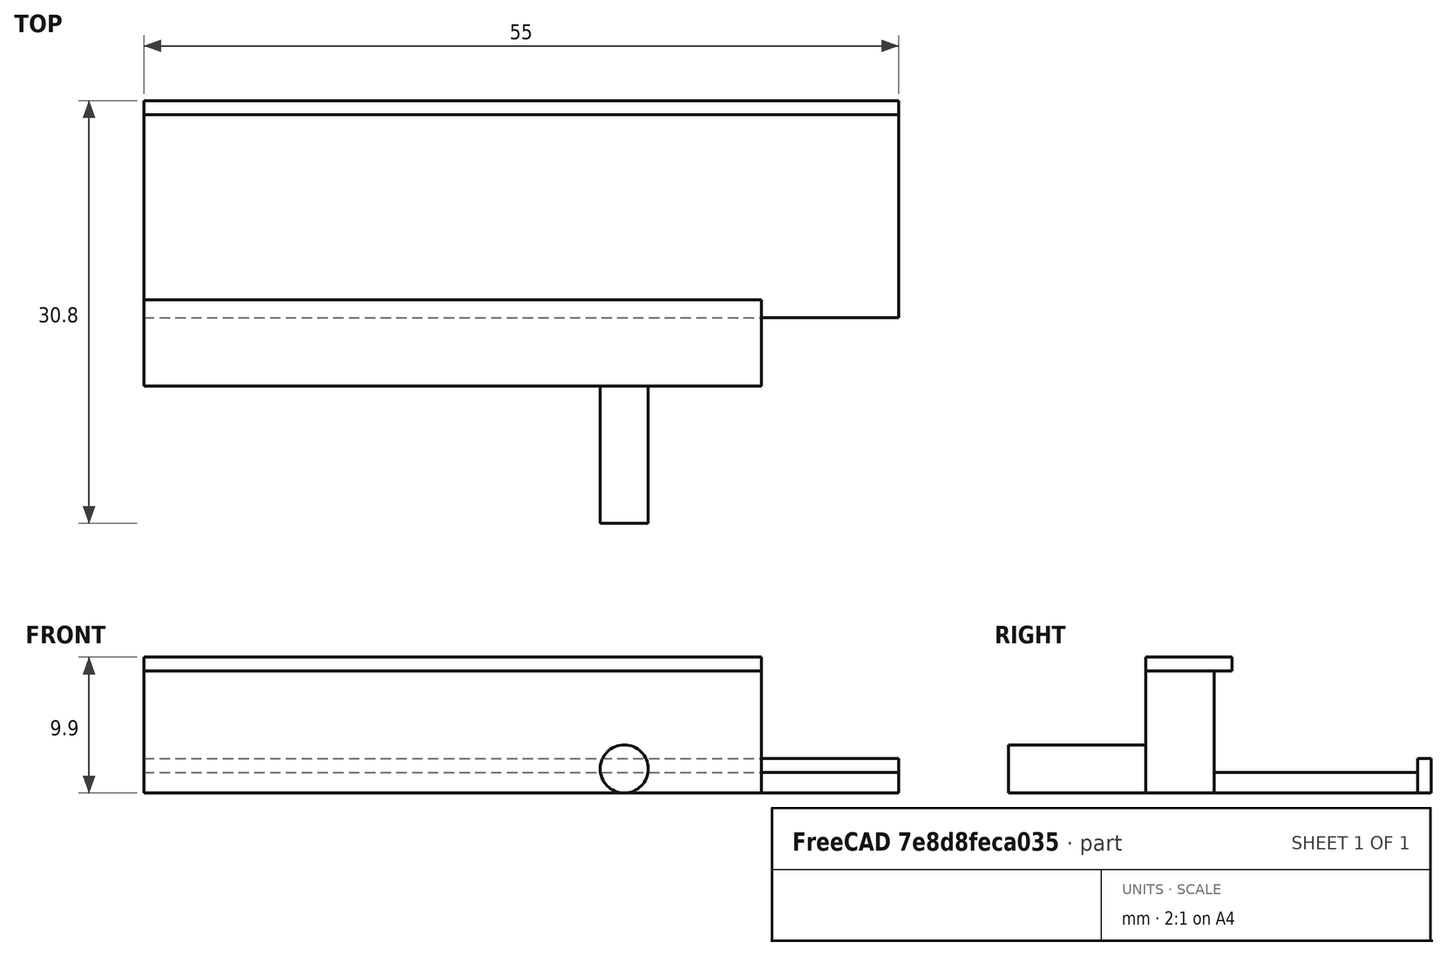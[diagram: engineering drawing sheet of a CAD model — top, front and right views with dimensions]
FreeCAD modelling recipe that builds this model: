
FCSTD DOCUMENT  (FreeCAD 0.21R33771 (Git))
Label: usb-support-1
License: All rights reserved
LicenseURL: http://en.wikipedia.org/wiki/All_rights_reserved
objects: Part::Box×4, Part::Cylinder×1
note: 5 computed .brp shape members not serialized (recipe doc carries the construction recipe); baked Part::Feature solids carry a one-line shape summary decoded from their .brp

FEATURE [Part::Box] Box  label="Cube"
  AttacherType = Attacher::AttachEngine3D
  Height = 8.9
  Length = 45
  Width = 5
FEATURE [Part::Box] Box001  label="Cube001"
  AttacherType = Attacher::AttachEngine3D
  Height = 1.5
  Length = 55
  Placement = pos=(0,5,0) rot=(0,0,1;0rad)
  Width = 14.8
FEATURE [Part::Box] Box002  label="Cube002"
  AttacherType = Attacher::AttachEngine3D
  Height = 2.5
  Length = 55
  Placement = pos=(0,19.8,0) rot=(0,0,1;0rad)
  Width = 1
FEATURE [Part::Box] Box003  label="Cube003"
  AttacherType = Attacher::AttachEngine3D
  Height = 1
  Length = 45
  Placement = pos=(0,0,8.9) rot=(0,0,1;0rad)
  Width = 6.3
FEATURE [Part::Cylinder] Cylinder
  Angle = 360
  AttacherType = Attacher::AttachEngine3D
  FirstAngle = 0
  Height = 10
  Placement = pos=(35,0,1.75) rot=(1,0,0;1.5708rad)
  Radius = 1.75
  SecondAngle = 0
